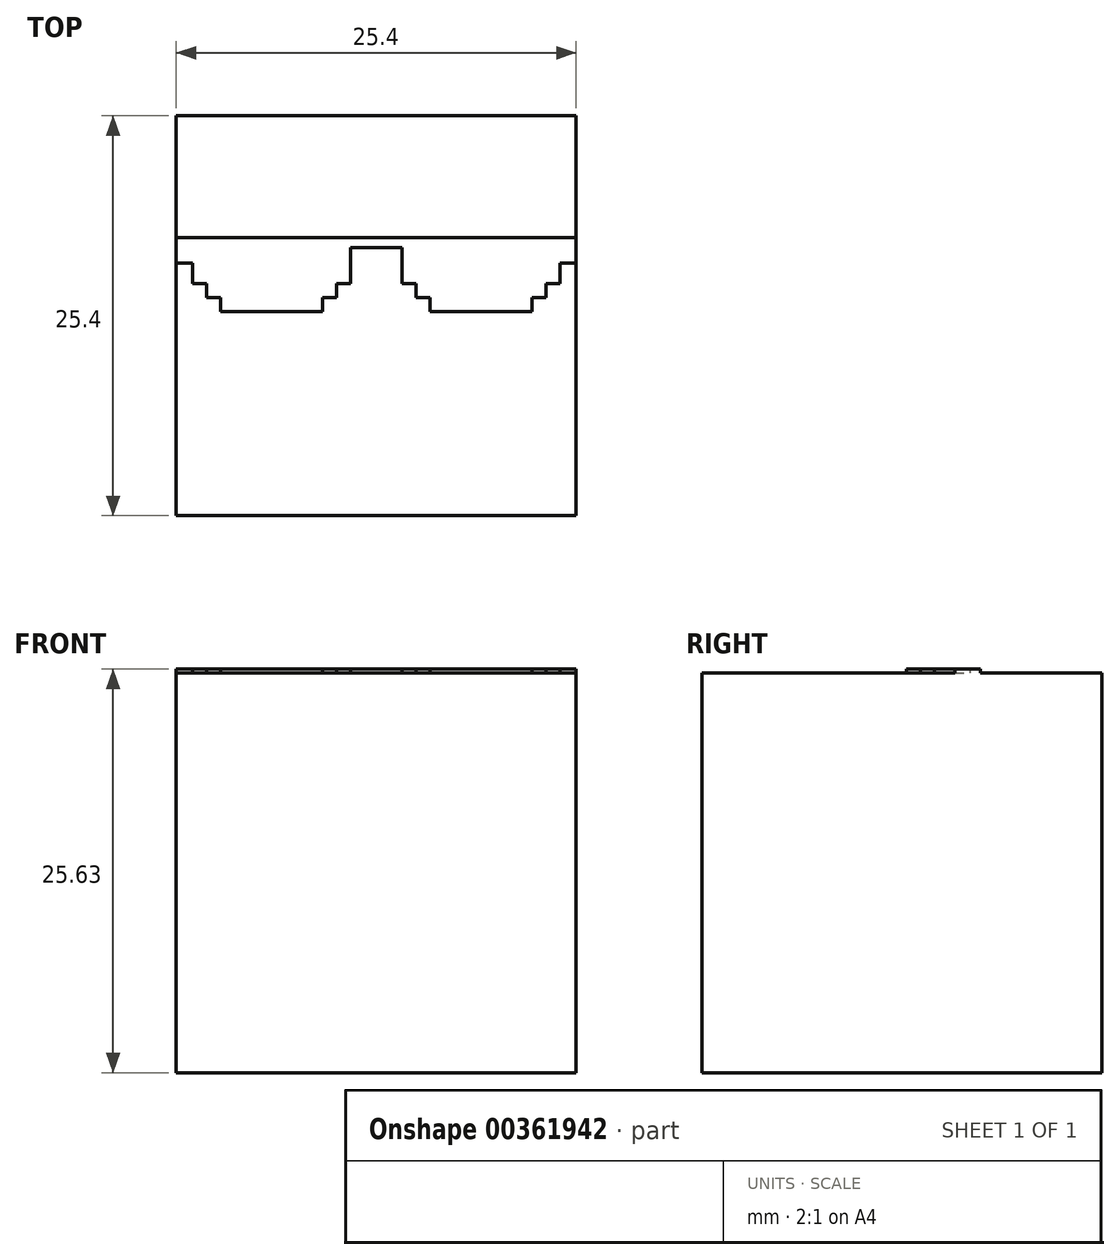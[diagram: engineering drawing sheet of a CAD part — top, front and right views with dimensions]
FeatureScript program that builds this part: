
annotation { "Feature Type Name" : "Feature", "Feature Type Description" : "" }
export const myFeature = defineFeature(function(context is Context, id is Id, definition is map)
    precondition{}
    {
        {
            var Q0;
            Q0=qCreatedBy(makeId("Top.planeOp"),FACE);
            var sketch = newSketch(context, id + "F0", { "sketchPlane" : qUnion([Q0])});
            skLineSegment(sketch, "E0", {"start": v(0, 0) * mm, "end": v(12.7, 0) * mm});
            skLineSegment(sketch, "E1", {"start": v(12.7, 0) * mm, "end": v(12.7, -25.4) * mm});
            skLineSegment(sketch, "E2.MirrorCS", {"start": v(0, 0) * mm, "end": v(-12.7, 0) * mm});
            skLineSegment(sketch, "E3.MirrorCS", {"start": v(-12.7, 0) * mm, "end": v(-12.7, -8.61) * mm});
            skLineSegment(sketch, "E4", {"start": v(-12.7, -25.4) * mm, "end": v(12.7, -25.4) * mm});
            skLineSegment(sketch, "E5.MirrorCS", {"start": v(12.7, -11.65) * mm, "end": v(12.7, -8.61) * mm});
            skPoint(sketch, "E6.start.orphan", {"position": v(-12.7, -11.65) * mm});
            skLineSegment(sketch, "E7.trimOffspring", {"start": v(-12.7, -11.65) * mm, "end": v(-12.7, -25.4) * mm});
            skPoint(sketch, "E8.end.orphan", {"position": v(-6.33, -8.61) * mm});
            skPoint(sketch, "E8.start.orphan", {"position": v(-9, -8.61) * mm});
            skPoint(sketch, "E9.end.orphan", {"position": v(-6.33, -11.65) * mm});
            skPoint(sketch, "E10.orphan", {"position": v(-9, -11.65) * mm});
            skPoint(sketch, "E11.end.orphan", {"position": v(-2.92, -11.65) * mm});
            skPoint(sketch, "E11.start.orphan", {"position": v(-2.92, -8.61) * mm});
            skPoint(sketch, "E12.MirrorCS.end.orphan", {"position": v(2.92, -11.65) * mm});
            skPoint(sketch, "E12.MirrorCS.start.orphan", {"position": v(2.92, -8.61) * mm});
            skPoint(sketch, "E13.MirrorCS.end.orphan", {"position": v(6.33, -8.61) * mm});
            skPoint(sketch, "E13.MirrorCS.start.orphan", {"position": v(6.33, -11.65) * mm});
            skPoint(sketch, "E14.MirrorCS.end.orphan", {"position": v(9, -11.65) * mm});
            skPoint(sketch, "E14.MirrorCS.start.orphan", {"position": v(9, -8.61) * mm});
            skPoint(sketch, "E15.orphan", {"position": v(12.7, -8.61) * mm});
            skPoint(sketch, "E16.orphan", {"position": v(12.7, -11.65) * mm});
            skLineSegment(sketch, "E17", {"start": v(-12.7, -8.61) * mm, "end": v(-12.7, -11.65) * mm});
            skSolve(sketch);
        }
        {
            var Q0;
            {var subQ3=sQuery(id+"F0.wireOp",EDGE,"E0");Q0=makeQuery(id+"F0.imprint","IMPRINT",FACE,{"disambiguationData":[TD([[makeQuery(id+"F0.imprint","IMPRINT",EDGE,{"derivedFrom":subQ3}),-1.0]])]});}
            extrude(context, id + "F1", {"entities" : qUnion([Q0]), "depth" : 25.4 * mm});
        }
        {
            var Q0;
            Q0=makeQuery(id+"F1.opExtrude","CAP_FACE",FACE,{"disambiguationData":[OSD([sQuery(id+"F0.wireOp",EDGE,"E0"),sQuery(id+"F0.wireOp",EDGE,"E1"),sQuery(id+"F0.wireOp",EDGE,"E2.MirrorCS"),sQuery(id+"F0.wireOp",EDGE,"E3.MirrorCS"),sQuery(id+"F0.wireOp",EDGE,"E4"),sQuery(id+"F0.wireOp",EDGE,"E5.MirrorCS"),sQuery(id+"F0.wireOp",EDGE,"E7.trimOffspring"),sQuery(id+"F0.wireOp",EDGE,"E17")])],"isStart":false});
            var sketch = newSketch(context, id + "F2", { "sketchPlane" : qUnion([Q0])});
            skLineSegment(sketch, "E18", {"start": v(-12.7, -7.73) * mm, "end": v(-2.53, -7.73) * mm});
            skLineSegment(sketch, "E19", {"start": v(-2.53, -10.66) * mm, "end": v(-2.53, -10.95) * mm});
            skLineSegment(sketch, "E20", {"start": v(-10.79, -10.95) * mm, "end": v(-12.7, -10.95) * mm});
            skLineSegment(sketch, "E21", {"start": v(-12.7, -10.95) * mm, "end": v(-12.7, -7.73) * mm});
            skLineSegment(sketch, "E22", {"start": v(-6.24, -7.73) * mm, "end": v(-9.4, -7.73) * mm});
            skLineSegment(sketch, "E23.MirrorCS", {"start": v(12.7, -10.95) * mm, "end": v(12.7, -7.73) * mm});
            skLineSegment(sketch, "E24.MirrorCS", {"start": v(12.7, -7.73) * mm, "end": v(2.53, -7.73) * mm});
            skLineSegment(sketch, "E25.MirrorCS", {"start": v(10.79, -10.95) * mm, "end": v(12.7, -10.95) * mm});
            skLineSegment(sketch, "E26.MirrorCS", {"start": v(2.53, -10.66) * mm, "end": v(2.53, -10.95) * mm});
            skLineSegment(sketch, "E27", {"start": v(-12.7, -7.73) * mm, "end": v(12.7, -7.73) * mm});
            skLineSegment(sketch, "E28", {"start": v(12.7, -7.73) * mm, "end": v(12.7, -9.34) * mm});
            skLineSegment(sketch, "E29", {"start": v(12.7, -9.34) * mm, "end": v(11.67, -9.34) * mm});
            skLineSegment(sketch, "E30", {"start": v(11.67, -9.34) * mm, "end": v(11.67, -10.66) * mm});
            skLineSegment(sketch, "E31", {"start": v(11.67, -10.66) * mm, "end": v(10.79, -10.66) * mm});
            skLineSegment(sketch, "E32", {"start": v(10.79, -10.66) * mm, "end": v(10.79, -11.55) * mm});
            skLineSegment(sketch, "E33", {"start": v(10.79, -11.55) * mm, "end": v(9.9, -11.55) * mm});
            skLineSegment(sketch, "E34", {"start": v(9.9, -11.55) * mm, "end": v(9.9, -12.44) * mm});
            skLineSegment(sketch, "E35", {"start": v(9.9, -12.44) * mm, "end": v(3.42, -12.44) * mm});
            skLineSegment(sketch, "E36", {"start": v(3.42, -12.44) * mm, "end": v(3.42, -11.55) * mm});
            skLineSegment(sketch, "E37", {"start": v(3.42, -11.55) * mm, "end": v(2.53, -11.55) * mm});
            skLineSegment(sketch, "E38", {"start": v(2.53, -11.55) * mm, "end": v(2.53, -10.66) * mm});
            skLineSegment(sketch, "E39", {"start": v(2.53, -10.66) * mm, "end": v(1.64, -10.66) * mm});
            skLineSegment(sketch, "E40", {"start": v(1.64, -10.66) * mm, "end": v(1.64, -8.39) * mm});
            skLineSegment(sketch, "E41.MirrorCS", {"start": v(-1.64, -10.66) * mm, "end": v(-1.64, -8.39) * mm});
            skLineSegment(sketch, "E42.MirrorCS", {"start": v(-2.53, -10.66) * mm, "end": v(-1.64, -10.66) * mm});
            skLineSegment(sketch, "E43.MirrorCS", {"start": v(-2.53, -11.55) * mm, "end": v(-2.53, -10.66) * mm});
            skLineSegment(sketch, "E44.MirrorCS", {"start": v(-3.42, -11.55) * mm, "end": v(-2.53, -11.55) * mm});
            skLineSegment(sketch, "E45.MirrorCS", {"start": v(-3.42, -12.44) * mm, "end": v(-3.42, -11.55) * mm});
            skLineSegment(sketch, "E46.MirrorCS", {"start": v(-9.9, -12.44) * mm, "end": v(-3.42, -12.44) * mm});
            skLineSegment(sketch, "E47.MirrorCS", {"start": v(-9.9, -11.55) * mm, "end": v(-9.9, -12.44) * mm});
            skLineSegment(sketch, "E48.MirrorCS", {"start": v(-10.79, -11.55) * mm, "end": v(-9.9, -11.55) * mm});
            skLineSegment(sketch, "E49.MirrorCS", {"start": v(-10.79, -10.66) * mm, "end": v(-10.79, -11.55) * mm});
            skLineSegment(sketch, "E50.MirrorCS", {"start": v(-11.67, -10.66) * mm, "end": v(-10.79, -10.66) * mm});
            skLineSegment(sketch, "E51.MirrorCS", {"start": v(-11.67, -9.34) * mm, "end": v(-11.67, -10.66) * mm});
            skLineSegment(sketch, "E52.MirrorCS", {"start": v(-12.7, -9.34) * mm, "end": v(-11.67, -9.34) * mm});
            skLineSegment(sketch, "E53", {"start": v(1.64, -8.39) * mm, "end": v(-1.64, -8.39) * mm});
            skPoint(sketch, "E54.orphan", {"position": v(-2.53, -7.73) * mm});
            skPoint(sketch, "E55.orphan", {"position": v(2.53, -7.73) * mm});
            skPoint(sketch, "E56.MirrorCS.end.orphan", {"position": v(6.24, -7.73) * mm});
            skPoint(sketch, "E57.MirrorCS.start.orphan", {"position": v(9.4, -7.73) * mm});
            skPoint(sketch, "E58.orphan", {"position": v(2.53, -10.95) * mm});
            skLineSegment(sketch, "E59", {"start": v(-12.7, -7.73) * mm, "end": v(-12.7, -9.34) * mm});
            skSolve(sketch);
        }
        {
            var Q0;
            Q0=makeQuery(id+"F2.imprint","IMPRINT",FACE,{"disambiguationData":[TD([[makeQuery(id+"F2.imprint","IMPRINT",EDGE,{"derivedFrom":sQuery(id+"F2.wireOp",EDGE,"E29")}),-1.0]])]});
            extrude(context, id + "F3", {"entities" : qUnion([Q0]), "operationType" : NewBodyOperationType.ADD, "depth" : 0.23 * mm});
        }
    });
